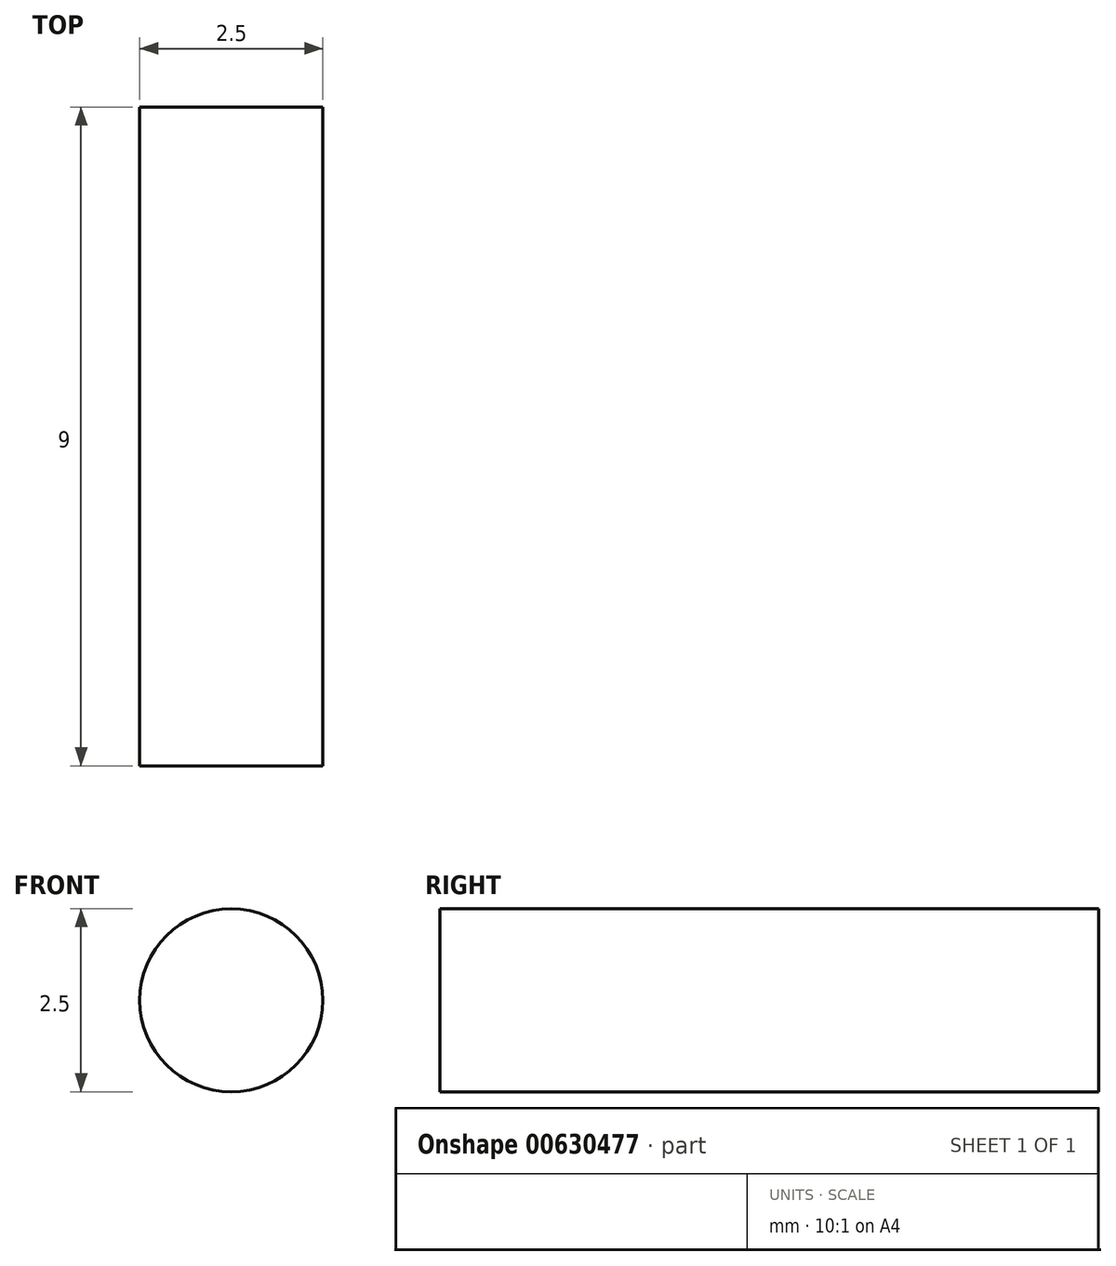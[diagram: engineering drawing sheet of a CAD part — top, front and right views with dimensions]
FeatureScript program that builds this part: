
annotation { "Feature Type Name" : "Feature", "Feature Type Description" : "" }
export const myFeature = defineFeature(function(context is Context, id is Id, definition is map)
    precondition{}
    {
        {
            var Q0;
            Q0=qCreatedBy(makeId("Front.planeOp"),FACE);
            var sketch = newSketch(context, id + "F0", { "sketchPlane" : qUnion([Q0])});
            skCircle(sketch, "E0", {"center": v(25.64, 14.57) * mm, "radius": 1.25 * mm});
            skSolve(sketch);
        }
        {
            var Q0;
            Q0 = qSketchRegion(id + "F0", true);
            extrude(context, id + "F1", {"entities" : qUnion([Q0]), "depth" : 9 * mm, "offsetDistance" : 25 * mm});
        }
    });
